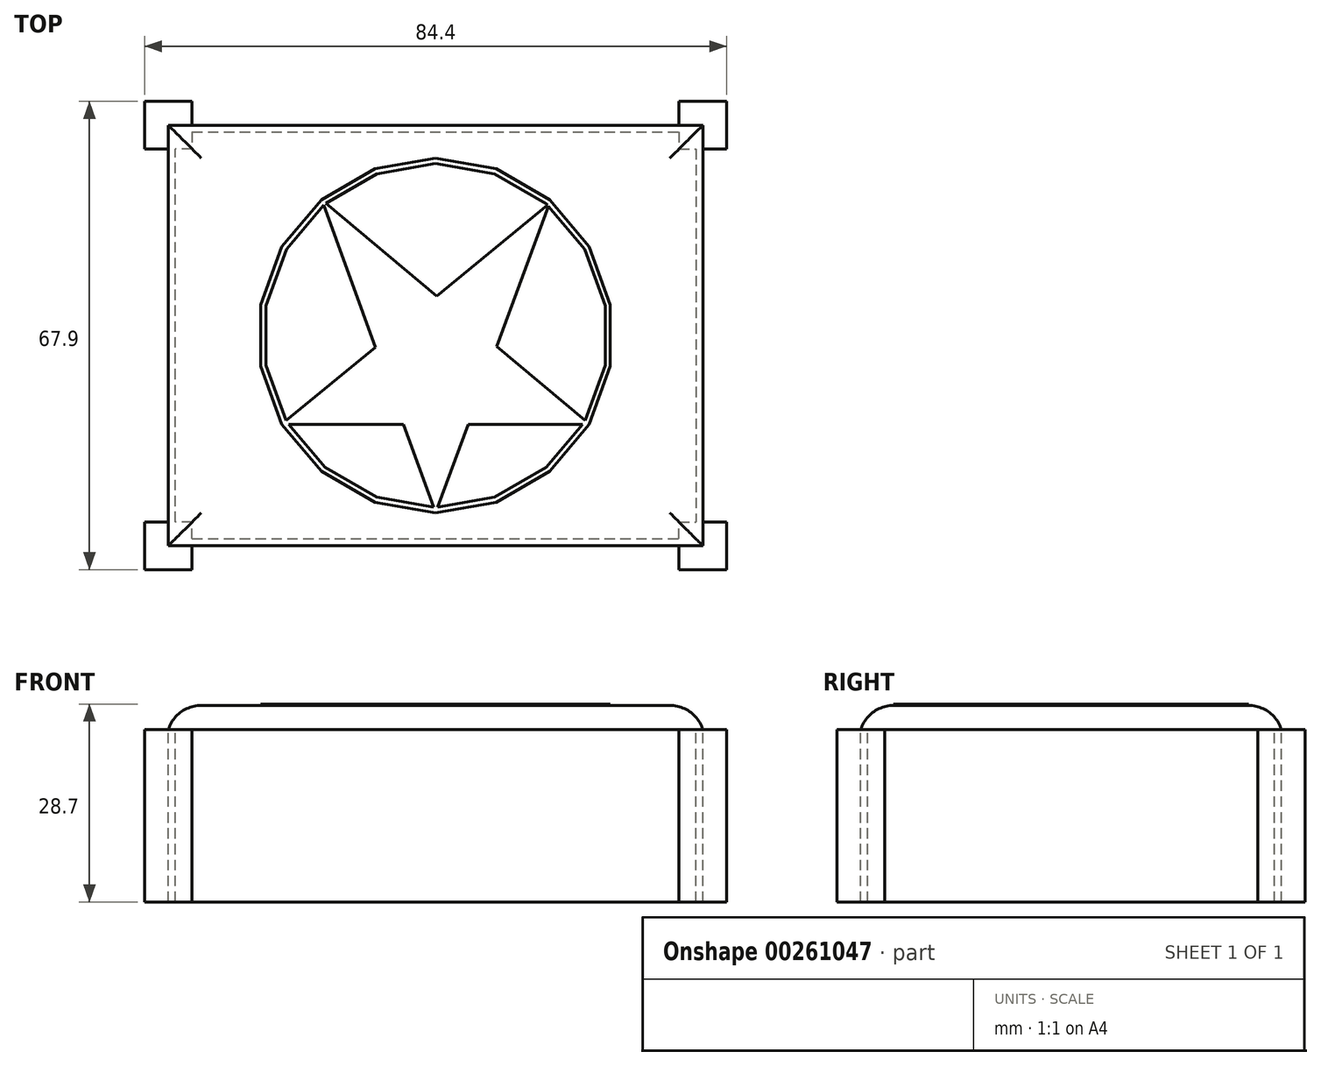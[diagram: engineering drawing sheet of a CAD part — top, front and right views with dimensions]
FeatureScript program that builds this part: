
annotation { "Feature Type Name" : "Feature", "Feature Type Description" : "" }
export const myFeature = defineFeature(function(context is Context, id is Id, definition is map)
    precondition{}
    {
        {
            var Q0;
            Q0=qCreatedBy(makeId("Top.planeOp"),FACE);
            var sketch = newSketch(context, id + "F0", { "sketchPlane" : qUnion([Q0])});
            skLineSegment(sketch, "E0.bottom", {"start": v(38.75, 30.5) * mm, "end": v(-38.75, 30.5) * mm});
            skLineSegment(sketch, "E0.top", {"start": v(38.75, -30.5) * mm, "end": v(-38.75, -30.5) * mm});
            skLineSegment(sketch, "E0.left", {"start": v(38.75, 30.5) * mm, "end": v(38.75, -30.5) * mm});
            skLineSegment(sketch, "E0.right", {"start": v(-38.75, 30.5) * mm, "end": v(-38.75, -30.5) * mm});
            skPoint(sketch, "E0.middle", {"position": v(0, 0) * mm});
            skSolve(sketch);
        }
        {
            var Q0;
            Q0 = qSketchRegion(id + "F0", true);
            extrude(context, id + "F1", {"entities" : qUnion([Q0]), "depth" : 3.5 * mm});
        }
        {
            var Q0;
            Q0=makeQuery(id+"F1.opExtrude","CAP_FACE",FACE,{"disambiguationData":[OSD([sQuery(id+"F0.wireOp",EDGE,"E0.bottom"),sQuery(id+"F0.wireOp",EDGE,"E0.top"),sQuery(id+"F0.wireOp",EDGE,"E0.left"),sQuery(id+"F0.wireOp",EDGE,"E0.right")])],"isStart":false});
            fillet(context, id + "F2", {"entities" : qUnion([Q0]), "radius" : 5 * mm, "tangentPropagation" : true, "allowEdgeOverflow" : false});
        }
        {
            var Q0;
            Q0=makeQuery(id+"F1.opExtrude","CAP_FACE",FACE,{"disambiguationData":[OSD([sQuery(id+"F0.wireOp",EDGE,"E0.bottom"),sQuery(id+"F0.wireOp",EDGE,"E0.top"),sQuery(id+"F0.wireOp",EDGE,"E0.left"),sQuery(id+"F0.wireOp",EDGE,"E0.right")])],"isStart":false});
            var sketch = newSketch(context, id + "F3", { "sketchPlane" : qUnion([Q0])});
            skLineSegment(sketch, "E1", {"start": v(0, -25.73) * mm, "end": v(-16.54, 19.71) * mm});
            skLineSegment(sketch, "E2", {"start": v(-16.54, 19.71) * mm, "end": v(22.28, -12.87) * mm});
            skLineSegment(sketch, "E3", {"start": v(22.28, -12.87) * mm, "end": v(-22.28, -12.87) * mm});
            skLineSegment(sketch, "E4", {"start": v(-22.28, -12.87) * mm, "end": v(16.54, 19.2) * mm});
            skLineSegment(sketch, "E5", {"start": v(16.54, 19.2) * mm, "end": v(0, -25.73) * mm});
            skCircle(sketch, "E6.cCircle", {"center": v(0, 0) * mm, "radius": 25.34 * mm, "construction": true});
            skLineSegment(sketch, "E6.0", {"start": v(8.8, 24.18) * mm, "end": v(16.54, 19.71) * mm});
            skLineSegment(sketch, "E6.1", {"start": v(16.54, 19.71) * mm, "end": v(22.28, 12.87) * mm});
            skLineSegment(sketch, "E6.2", {"start": v(22.28, 12.87) * mm, "end": v(25.34, 4.47) * mm});
            skLineSegment(sketch, "E6.3", {"start": v(25.34, 4.47) * mm, "end": v(25.34, -4.47) * mm});
            skLineSegment(sketch, "E6.4", {"start": v(25.34, -4.47) * mm, "end": v(22.28, -12.87) * mm});
            skLineSegment(sketch, "E6.5", {"start": v(22.28, -12.87) * mm, "end": v(16.54, -19.71) * mm});
            skLineSegment(sketch, "E6.6", {"start": v(16.54, -19.71) * mm, "end": v(8.8, -24.18) * mm});
            skLineSegment(sketch, "E6.7", {"start": v(8.8, -24.18) * mm, "end": v(0, -25.73) * mm});
            skLineSegment(sketch, "E6.8", {"start": v(0, -25.73) * mm, "end": v(-8.8, -24.18) * mm});
            skLineSegment(sketch, "E6.9", {"start": v(-8.8, -24.18) * mm, "end": v(-16.54, -19.71) * mm});
            skLineSegment(sketch, "E6.10", {"start": v(-16.54, -19.71) * mm, "end": v(-22.28, -12.87) * mm});
            skLineSegment(sketch, "E6.11", {"start": v(-22.28, -12.87) * mm, "end": v(-25.34, -4.47) * mm});
            skLineSegment(sketch, "E6.12", {"start": v(-25.34, -4.47) * mm, "end": v(-25.34, 4.47) * mm});
            skLineSegment(sketch, "E6.13", {"start": v(-25.34, 4.47) * mm, "end": v(-22.28, 12.87) * mm});
            skLineSegment(sketch, "E6.14", {"start": v(-22.28, 12.87) * mm, "end": v(-16.54, 19.71) * mm});
            skLineSegment(sketch, "E6.15", {"start": v(-16.54, 19.71) * mm, "end": v(-8.8, 24.18) * mm});
            skLineSegment(sketch, "E6.16", {"start": v(-8.8, 24.18) * mm, "end": v(0, 25.73) * mm});
            skLineSegment(sketch, "E6.17", {"start": v(0, 25.73) * mm, "end": v(8.8, 24.18) * mm});
            skPoint(sketch, "E6.0.midPoint", {"position": v(12.67, 21.94) * mm});
            skCircle(sketch, "E7.cCircle", {"center": v(0, 0) * mm, "radius": 24.58 * mm, "construction": true});
            skLineSegment(sketch, "E7.0", {"start": v(8.54, 23.46) * mm, "end": v(16.04, 19.12) * mm});
            skLineSegment(sketch, "E7.1", {"start": v(16.04, 19.12) * mm, "end": v(21.62, 12.48) * mm});
            skLineSegment(sketch, "E7.2", {"start": v(21.62, 12.48) * mm, "end": v(24.58, 4.33) * mm});
            skLineSegment(sketch, "E7.3", {"start": v(24.58, 4.33) * mm, "end": v(24.58, -4.33) * mm});
            skLineSegment(sketch, "E7.4", {"start": v(24.58, -4.33) * mm, "end": v(21.62, -12.48) * mm});
            skLineSegment(sketch, "E7.5", {"start": v(21.62, -12.48) * mm, "end": v(16.04, -19.12) * mm});
            skLineSegment(sketch, "E7.6", {"start": v(16.04, -19.12) * mm, "end": v(8.54, -23.46) * mm});
            skLineSegment(sketch, "E7.7", {"start": v(8.54, -23.46) * mm, "end": v(0, -24.96) * mm});
            skLineSegment(sketch, "E7.8", {"start": v(0, -24.96) * mm, "end": v(-8.54, -23.46) * mm});
            skLineSegment(sketch, "E7.9", {"start": v(-8.54, -23.46) * mm, "end": v(-16.04, -19.12) * mm});
            skLineSegment(sketch, "E7.10", {"start": v(-16.04, -19.12) * mm, "end": v(-21.62, -12.48) * mm});
            skLineSegment(sketch, "E7.11", {"start": v(-21.62, -12.48) * mm, "end": v(-24.58, -4.33) * mm});
            skLineSegment(sketch, "E7.12", {"start": v(-24.58, -4.33) * mm, "end": v(-24.58, 4.33) * mm});
            skLineSegment(sketch, "E7.13", {"start": v(-24.58, 4.33) * mm, "end": v(-21.62, 12.48) * mm});
            skLineSegment(sketch, "E7.14", {"start": v(-21.62, 12.48) * mm, "end": v(-16.04, 19.12) * mm});
            skLineSegment(sketch, "E7.15", {"start": v(-16.04, 19.12) * mm, "end": v(-8.54, 23.46) * mm});
            skLineSegment(sketch, "E7.16", {"start": v(-8.54, 23.46) * mm, "end": v(0, 24.96) * mm});
            skLineSegment(sketch, "E7.17", {"start": v(0, 24.96) * mm, "end": v(8.54, 23.46) * mm});
            skPoint(sketch, "E7.0.midPoint", {"position": v(12.3, 21.29) * mm});
            skSolve(sketch);
        }
        {
            var Q0;
            Q0=makeQuery(id+"F1.opExtrude","CAP_FACE",FACE,{"disambiguationData":[OSD([sQuery(id+"F0.wireOp",EDGE,"E0.bottom"),sQuery(id+"F0.wireOp",EDGE,"E0.top"),sQuery(id+"F0.wireOp",EDGE,"E0.left"),sQuery(id+"F0.wireOp",EDGE,"E0.right")])],"isStart":true});
            var sketch = newSketch(context, id + "F4", { "sketchPlane" : qUnion([Q0])});
            skLineSegment(sketch, "E8.bottom", {"start": v(-38.75, 30.5) * mm, "end": v(-37.75, 30.5) * mm});
            skLineSegment(sketch, "E8.top", {"start": v(-38.75, -30.5) * mm, "end": v(-37.75, -30.5) * mm});
            skLineSegment(sketch, "E8.left", {"start": v(-38.75, 30.5) * mm, "end": v(-38.75, -30.5) * mm});
            skLineSegment(sketch, "E9.bottom", {"start": v(38.75, 30.5) * mm, "end": v(37.75, 30.5) * mm});
            skLineSegment(sketch, "E9.top", {"start": v(38.75, -30.5) * mm, "end": v(37.75, -30.5) * mm});
            skLineSegment(sketch, "E9.left", {"start": v(38.75, 30.5) * mm, "end": v(38.75, -30.5) * mm});
            skLineSegment(sketch, "E10.bottom", {"start": v(-38.75, 30.5) * mm, "end": v(38.75, 30.5) * mm});
            skLineSegment(sketch, "E10.left", {"start": v(-38.75, 30.5) * mm, "end": v(-38.75, 29.5) * mm});
            skLineSegment(sketch, "E10.right", {"start": v(38.75, 30.5) * mm, "end": v(38.75, 29.5) * mm});
            skLineSegment(sketch, "E11.bottom", {"start": v(38.75, -30.5) * mm, "end": v(-38.75, -30.5) * mm});
            skLineSegment(sketch, "E11.left", {"start": v(38.75, -30.5) * mm, "end": v(38.75, -29.5) * mm});
            skLineSegment(sketch, "E11.right", {"start": v(-38.75, -30.5) * mm, "end": v(-38.75, -29.5) * mm});
            skLineSegment(sketch, "E12", {"start": v(-35.3, 29.5) * mm, "end": v(35.3, 29.5) * mm});
            skLineSegment(sketch, "E13", {"start": v(-37.75, 27.05) * mm, "end": v(-37.75, -27.75) * mm});
            skLineSegment(sketch, "E14", {"start": v(-36.2, -29.5) * mm, "end": v(36.64, -29.5) * mm});
            skLineSegment(sketch, "E15", {"start": v(37.75, -28.62) * mm, "end": v(37.75, 27.7) * mm});
            skLineSegment(sketch, "E16.bottom", {"start": v(-35.3, 33.95) * mm, "end": v(-42.2, 33.95) * mm});
            skLineSegment(sketch, "E16.top", {"start": v(-35.3, 27.05) * mm, "end": v(-37.75, 27.05) * mm});
            skLineSegment(sketch, "E16.left", {"start": v(-35.3, 33.95) * mm, "end": v(-35.3, 30.5) * mm});
            skLineSegment(sketch, "E16.right", {"start": v(-42.2, 33.95) * mm, "end": v(-42.2, 27.05) * mm});
            skPoint(sketch, "E16.middle", {"position": v(-38.75, 30.5) * mm});
            skLineSegment(sketch, "E17.trimOffspring", {"start": v(-35.3, 29.5) * mm, "end": v(-35.3, 27.05) * mm});
            skLineSegment(sketch, "E18.trimOffspring", {"start": v(-38.75, 27.05) * mm, "end": v(-42.2, 27.05) * mm});
            skLineSegment(sketch, "E19.MirrorCS", {"start": v(35.3, 33.95) * mm, "end": v(42.2, 33.95) * mm});
            skLineSegment(sketch, "E20.MirrorCS", {"start": v(42.2, 33.95) * mm, "end": v(42.2, 27.05) * mm});
            skLineSegment(sketch, "E21.MirrorCS", {"start": v(38.75, 27.05) * mm, "end": v(42.2, 27.05) * mm});
            skLineSegment(sketch, "E22.MirrorCS", {"start": v(35.3, 29.5) * mm, "end": v(35.3, 27.05) * mm});
            skLineSegment(sketch, "E23.MirrorCS", {"start": v(35.3, 33.95) * mm, "end": v(35.3, 30.5) * mm});
            skLineSegment(sketch, "E24.MirrorCS", {"start": v(35.3, 27.05) * mm, "end": v(37.75, 27.05) * mm});
            skLineSegment(sketch, "E25", {"start": v(37.75, 27.7) * mm, "end": v(37.75, 27.05) * mm});
            skLineSegment(sketch, "E26.MirrorCS", {"start": v(38.75, -27.05) * mm, "end": v(42.2, -27.05) * mm});
            skLineSegment(sketch, "E27.MirrorCS", {"start": v(42.2, -33.95) * mm, "end": v(42.2, -27.05) * mm});
            skLineSegment(sketch, "E28.MirrorCS", {"start": v(35.3, -33.95) * mm, "end": v(42.2, -33.95) * mm});
            skLineSegment(sketch, "E29.MirrorCS", {"start": v(35.3, -33.95) * mm, "end": v(35.3, -30.5) * mm});
            skLineSegment(sketch, "E30.MirrorCS", {"start": v(35.3, -29.5) * mm, "end": v(35.3, -27.05) * mm});
            skLineSegment(sketch, "E31.MirrorCS", {"start": v(35.3, -27.05) * mm, "end": v(37.75, -27.05) * mm});
            skLineSegment(sketch, "E32.MirrorCS", {"start": v(-35.3, -27.05) * mm, "end": v(-37.75, -27.05) * mm});
            skLineSegment(sketch, "E33.MirrorCS", {"start": v(-35.3, -29.5) * mm, "end": v(-35.3, -27.05) * mm});
            skLineSegment(sketch, "E34.MirrorCS", {"start": v(-35.3, -33.95) * mm, "end": v(-35.3, -30.5) * mm});
            skLineSegment(sketch, "E35.MirrorCS", {"start": v(-35.3, -33.95) * mm, "end": v(-42.2, -33.95) * mm});
            skLineSegment(sketch, "E36.MirrorCS", {"start": v(-42.2, -33.95) * mm, "end": v(-42.2, -27.05) * mm});
            skLineSegment(sketch, "E37.MirrorCS", {"start": v(-38.75, -27.05) * mm, "end": v(-42.2, -27.05) * mm});
            skLineSegment(sketch, "E38", {"start": v(-37.75, -27.05) * mm, "end": v(-37.75, -27.75) * mm});
            skLineSegment(sketch, "E39", {"start": v(-36.2, -29.5) * mm, "end": v(-35.3, -29.5) * mm});
            skSolve(sketch);
        }
        {
            var Q0;
            Q0 = qSketchRegion(id + "F4", true);
            extrude(context, id + "F5", {"entities" : qUnion([Q0]), "operationType" : NewBodyOperationType.ADD, "depth" : 25 * mm});
        }
        {
            var Q0;
            {var subQ1=sQuery(id+"F3.wireOp",EDGE,"E1");var subQ3=sQuery(id+"F3.wireOp",EDGE,"E4");var subQ4=makeQuery(id+"F3.imprint","INTERSECT",VERTEX,{"derivedFrom":[subQ1,subQ3]});Q0=makeQuery(id+"F3.imprint","IMPRINT",FACE,{"disambiguationData":[TD([[makeQuery(id+"F3.imprint","IMPRINT",EDGE,{"disambiguationData":[TD([[subQ4,-1.0]])],"derivedFrom":subQ3}),1.0]])]});}
            var Q1;
            {var subQ0=sQuery(id+"F3.wireOp",EDGE,"E3");var subQ1=sQuery(id+"F3.wireOp",EDGE,"E1");var subQ2=makeQuery(id+"F3.imprint","INTERSECT",VERTEX,{"derivedFrom":[subQ1,subQ0]});Q1=makeQuery(id+"F3.imprint","IMPRINT",FACE,{"disambiguationData":[TD([[makeQuery(id+"F3.imprint","IMPRINT",EDGE,{"disambiguationData":[TD([[subQ2,-1.0]])],"derivedFrom":subQ1}),1.0]])]});}
            var Q2;
            {var subQ1=sQuery(id+"F3.wireOp",EDGE,"E1");var subQ4=sQuery(id+"F3.wireOp",EDGE,"E3");var subQ5=makeQuery(id+"F3.imprint","INTERSECT",VERTEX,{"derivedFrom":[subQ1,subQ4]});Q2=makeQuery(id+"F3.imprint","IMPRINT",FACE,{"disambiguationData":[TD([[makeQuery(id+"F3.imprint","IMPRINT",EDGE,{"disambiguationData":[TD([[subQ5,1.0]])],"derivedFrom":subQ4}),1.0]])]});}
            var Q3;
            {var subQ1=sQuery(id+"F3.wireOp",EDGE,"E2");var subQ3=sQuery(id+"F3.wireOp",EDGE,"E5");var subQ4=makeQuery(id+"F3.imprint","INTERSECT",VERTEX,{"derivedFrom":[subQ1,subQ3]});Q3=makeQuery(id+"F3.imprint","IMPRINT",FACE,{"disambiguationData":[TD([[makeQuery(id+"F3.imprint","IMPRINT",EDGE,{"disambiguationData":[TD([[subQ4,-1.0]])],"derivedFrom":subQ3}),1.0]])]});}
            var Q4;
            {var subQ0=sQuery(id+"F3.wireOp",EDGE,"E4");var subQ1=sQuery(id+"F3.wireOp",EDGE,"E2");var subQ2=makeQuery(id+"F3.imprint","INTERSECT",VERTEX,{"derivedFrom":[subQ1,subQ0]});Q4=makeQuery(id+"F3.imprint","IMPRINT",FACE,{"disambiguationData":[TD([[makeQuery(id+"F3.imprint","IMPRINT",EDGE,{"disambiguationData":[TD([[subQ2,-1.0]])],"derivedFrom":subQ1}),1.0]])]});}
            var Q5;
            {var subQ0=sQuery(id+"F3.wireOp",EDGE,"E6.11");Q5=makeQuery(id+"F3.imprint","IMPRINT",FACE,{"disambiguationData":[TD([[makeQuery(id+"F3.imprint","IMPRINT",EDGE,{"derivedFrom":subQ0}),-1.0]])]});}
            var Q6;
            {var subQ0=sQuery(id+"F3.wireOp",EDGE,"E6.5");Q6=makeQuery(id+"F3.imprint","IMPRINT",FACE,{"disambiguationData":[TD([[makeQuery(id+"F3.imprint","IMPRINT",EDGE,{"derivedFrom":subQ0}),-1.0]])]});}
            var Q7;
            {var subQ0=sQuery(id+"F3.wireOp",EDGE,"E6.8");Q7=makeQuery(id+"F3.imprint","IMPRINT",FACE,{"disambiguationData":[TD([[makeQuery(id+"F3.imprint","IMPRINT",EDGE,{"derivedFrom":subQ0}),-1.0]])]});}
            var Q8;
            {var subQ3=sQuery(id+"F3.wireOp",EDGE,"E7.10");var subQ5=sQuery(id+"F3.wireOp",EDGE,"E7.11");var subQ6=makeQuery(id+"F3.imprint","INTERSECT",VERTEX,{"derivedFrom":[subQ3,subQ5]});Q8=makeQuery(id+"F3.imprint","IMPRINT",FACE,{"disambiguationData":[TD([[makeQuery(id+"F3.imprint","IMPRINT",EDGE,{"disambiguationData":[TD([[subQ6,1.0]])],"derivedFrom":subQ3}),1.0]])]});}
            var Q9;
            {var subQ3=sQuery(id+"F3.wireOp",EDGE,"E7.14");var subQ5=sQuery(id+"F3.wireOp",EDGE,"E7.15");var subQ7=makeQuery(id+"F3.imprint","INTERSECT",VERTEX,{"derivedFrom":[subQ3,subQ5]});Q9=makeQuery(id+"F3.imprint","IMPRINT",FACE,{"disambiguationData":[TD([[makeQuery(id+"F3.imprint","IMPRINT",EDGE,{"disambiguationData":[TD([[subQ7,1.0]])],"derivedFrom":subQ3}),1.0]])]});}
            var Q10;
            Q10=makeQuery(id+"F3.imprint","IMPRINT",FACE,{"disambiguationData":[TD([[makeQuery(id+"F3.imprint","IMPRINT",EDGE,{"derivedFrom":sQuery(id+"F3.wireOp",EDGE,"E6.0")}),-1.0]])]});
            var Q11;
            {var subQ0=sQuery(id+"F3.wireOp",EDGE,"E5");var subQ1=sQuery(id+"F3.wireOp",EDGE,"E4");var subQ2=makeQuery(id+"F3.imprint","INTERSECT",VERTEX,{"derivedFrom":[subQ1,subQ0]});Q11=makeQuery(id+"F3.imprint","IMPRINT",FACE,{"disambiguationData":[TD([[makeQuery(id+"F3.imprint","IMPRINT",EDGE,{"disambiguationData":[TD([[subQ2,1.0]])],"derivedFrom":subQ1}),-1.0]])]});}
            var Q12;
            {var subQ3=sQuery(id+"F3.wireOp",EDGE,"E7.4");var subQ5=sQuery(id+"F3.wireOp",EDGE,"E7.5");var subQ6=makeQuery(id+"F3.imprint","INTERSECT",VERTEX,{"derivedFrom":[subQ3,subQ5]});Q12=makeQuery(id+"F3.imprint","IMPRINT",FACE,{"disambiguationData":[TD([[makeQuery(id+"F3.imprint","IMPRINT",EDGE,{"disambiguationData":[TD([[subQ6,1.0]])],"derivedFrom":subQ3}),1.0]])]});}
            var Q13;
            {var subQ4=sQuery(id+"F3.wireOp",EDGE,"E7.8");var subQ6=sQuery(id+"F3.wireOp",EDGE,"E7.7");var subQ8=makeQuery(id+"F3.imprint","INTERSECT",VERTEX,{"derivedFrom":[subQ6,subQ4]});Q13=makeQuery(id+"F3.imprint","IMPRINT",FACE,{"disambiguationData":[TD([[makeQuery(id+"F3.imprint","IMPRINT",EDGE,{"disambiguationData":[TD([[subQ8,1.0]])],"derivedFrom":subQ6}),1.0]])]});}
            var Q14;
            {var subQ1=sQuery(id+"F3.wireOp",EDGE,"E1");var subQ5=sQuery(id+"F3.wireOp",EDGE,"E3");var subQ6=makeQuery(id+"F3.imprint","INTERSECT",VERTEX,{"derivedFrom":[subQ1,subQ5]});Q14=makeQuery(id+"F3.imprint","IMPRINT",FACE,{"disambiguationData":[TD([[makeQuery(id+"F3.imprint","IMPRINT",EDGE,{"disambiguationData":[TD([[subQ6,-1.0]])],"derivedFrom":subQ1}),-1.0]])]});}
            extrude(context, id + "F6", {"entities" : qUnion([Q0, Q1, Q2, Q3, Q4, Q5, Q6, Q7, Q8, Q9, Q10, Q11, Q12, Q13, Q14]), "operationType" : NewBodyOperationType.ADD, "depth" : 0.2 * mm});
        }
    });
